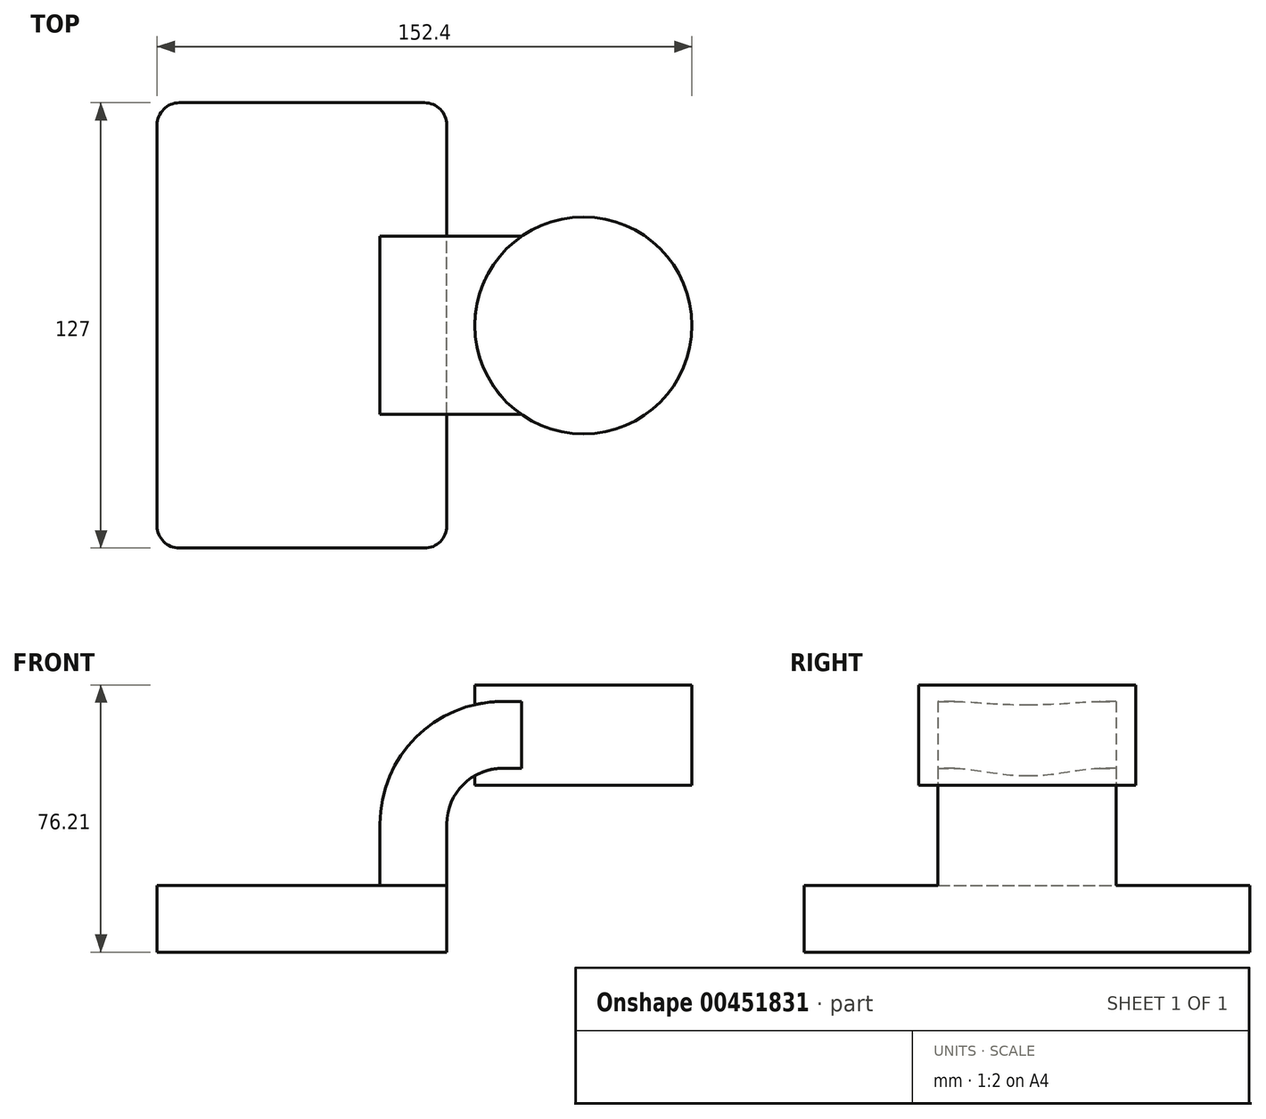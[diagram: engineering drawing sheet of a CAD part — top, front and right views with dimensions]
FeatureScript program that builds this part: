
annotation { "Feature Type Name" : "Feature", "Feature Type Description" : "" }
export const myFeature = defineFeature(function(context is Context, id is Id, definition is map)
    precondition{}
    {
        {
            var Q0;
            Q0=qCreatedBy(makeId("Front.planeOp"),FACE);
            var sketch = newSketch(context, id + "F0", { "sketchPlane" : qUnion([Q0])});
            skLineSegment(sketch, "E0.bottom", {"start": v(-41.28, -9.53) * mm, "end": v(41.28, -9.53) * mm});
            skLineSegment(sketch, "E0.top", {"start": v(-41.28, 9.53) * mm, "end": v(41.28, 9.53) * mm});
            skLineSegment(sketch, "E0.left", {"start": v(-41.28, -9.53) * mm, "end": v(-41.28, 9.53) * mm});
            skLineSegment(sketch, "E0.right", {"start": v(41.28, -9.53) * mm, "end": v(41.28, 9.53) * mm});
            skPoint(sketch, "E0.middle", {"position": v(0, 0) * mm});
            skLineSegment(sketch, "E1.bottom", {"start": v(60.32, 38.1) * mm, "end": v(111.12, 38.1) * mm});
            skLineSegment(sketch, "E1.top", {"start": v(60.32, 66.67) * mm, "end": v(111.12, 66.67) * mm});
            skLineSegment(sketch, "E1.left", {"start": v(60.32, 38.1) * mm, "end": v(60.32, 66.67) * mm});
            skLineSegment(sketch, "E1.right", {"start": v(111.12, 38.1) * mm, "end": v(111.12, 66.67) * mm});
            skPoint(sketch, "E1.middle", {"position": v(85.72, 52.39) * mm});
            skLineSegment(sketch, "E2", {"start": v(41.27, 9.53) * mm, "end": v(41.27, 27) * mm});
            skArc(sketch, "E3", {"start": v(41.27, 27) * mm, "mid": v(45.92, 38.23) * mm, "end": v(57.15, 42.88) * mm});
            skLineSegment(sketch, "E4", {"start": v(57.15, 42.88) * mm, "end": v(80.2, 42.88) * mm});
            skLineSegment(sketch, "E5.0", {"start": v(57.15, 61.93) * mm, "end": v(80.2, 61.93) * mm});
            skArc(sketch, "E5.1", {"start": v(22.23, 27) * mm, "mid": v(32.45, 51.7) * mm, "end": v(57.15, 61.93) * mm});
            skLineSegment(sketch, "E5.2", {"start": v(22.22, 9.53) * mm, "end": v(22.22, 27) * mm});
            skFitSpline(sketch, "E6", {"points": [v(-41.28, 9.53) * mm, v(57.15, 61.93) * mm], "startDerivative": vector(30.5, 108.58) * mm, "endDerivative": vector(110.68, -5.7) * mm});
            skLineSegment(sketch, "E7", {"start": v(80.2, 38.1) * mm, "end": v(80.2, 66.67) * mm});
            skSolve(sketch);
        }
        {
            var Q0;
            Q0=makeQuery(id+"F0.imprint","IMPRINT",FACE,{"disambiguationData":[TD([[makeQuery(id+"F0.imprint","IMPRINT",EDGE,{"derivedFrom":sQuery(id+"F0.wireOp",EDGE,"E0.bottom")}),1.0]])]});
            extrude(context, id + "F1", {"entities" : qUnion([Q0]), "endBound" : BoundingType.SYMMETRIC, "depth" : 127 * mm});
        }
        {
            var Q0;
            {var subQ1=sQuery(id+"F0.wireOp",EDGE,"E2");Q0=makeQuery(id+"F0.imprint","IMPRINT",FACE,{"disambiguationData":[TD([[makeQuery(id+"F0.imprint","IMPRINT",EDGE,{"derivedFrom":subQ1}),1.0]])]});}
            var Q1;
            {var subQ0=sQuery(id+"F0.wireOp",EDGE,"E4");var subQ1=sQuery(id+"F0.wireOp",EDGE,"E1.left");var subQ2=makeQuery(id+"F0.imprint","INTERSECT",VERTEX,{"derivedFrom":[subQ1,subQ0]});Q1=makeQuery(id+"F0.imprint","IMPRINT",FACE,{"disambiguationData":[TD([[makeQuery(id+"F0.imprint","IMPRINT",EDGE,{"disambiguationData":[TD([[subQ2,-1.0]])],"derivedFrom":subQ1}),-1.0]])]});}
            extrude(context, id + "F2", {"entities" : qUnion([Q0, Q1]), "operationType" : NewBodyOperationType.ADD, "endBound" : BoundingType.SYMMETRIC, "depth" : 50.8 * mm});
        }
        {
            var Q0;
            Q0=makeQuery(id+"F0.imprint","IMPRINT",FACE,{"disambiguationData":[TD([[makeQuery(id+"F0.imprint","IMPRINT",EDGE,{"derivedFrom":sQuery(id+"F0.wireOp",EDGE,"E5.1")}),1.0]])]});
            extrude(context, id + "F3", {"entities" : qUnion([Q0]), "operationType" : NewBodyOperationType.ADD, "depth" : 15.88 * mm});
        }
        {
            var Q0;
            {var subQ4=sQuery(id+"F0.wireOp",EDGE,"E1.right");Q0=makeQuery(id+"F0.imprint","IMPRINT",FACE,{"disambiguationData":[TD([[makeQuery(id+"F0.imprint","IMPRINT",EDGE,{"derivedFrom":subQ4}),1.0]])]});}
            var Q1;
            Q1=sQuery(id+"F0.wireOp",EDGE,"E7");
            revolve(context, id + "F4", {"operationType" : NewBodyOperationType.ADD, "entities" : qUnion([Q0]), "axis" : qUnion([Q1]), "revolveType" : RevolveType.FULL});
        }
        {
            var Q0;
            Q0=makeQuery(id+"F1.opExtrude","CAP_EDGE",EDGE,{"disambiguationData":[OSD([sQuery(id+"F0.wireOp",EDGE,"E0.left")])],"isStart":false});
            var Q1;
            Q1=makeQuery(id+"F1.opExtrude","CAP_EDGE",EDGE,{"disambiguationData":[OSD([sQuery(id+"F0.wireOp",EDGE,"E0.right")])],"isStart":false});
            var Q2;
            Q2=makeQuery(id+"F1.opExtrude","CAP_EDGE",EDGE,{"disambiguationData":[OSD([sQuery(id+"F0.wireOp",EDGE,"E0.right")])],"isStart":true});
            var Q3;
            Q3=makeQuery(id+"F1.opExtrude","CAP_EDGE",EDGE,{"disambiguationData":[OSD([sQuery(id+"F0.wireOp",EDGE,"E0.left")])],"isStart":true});
            fillet(context, id + "F5", {"entities" : qUnion([Q0, Q1, Q2, Q3]), "radius" : 6.35 * mm, "tangentPropagation" : true, "allowEdgeOverflow" : false});
        }
    });
